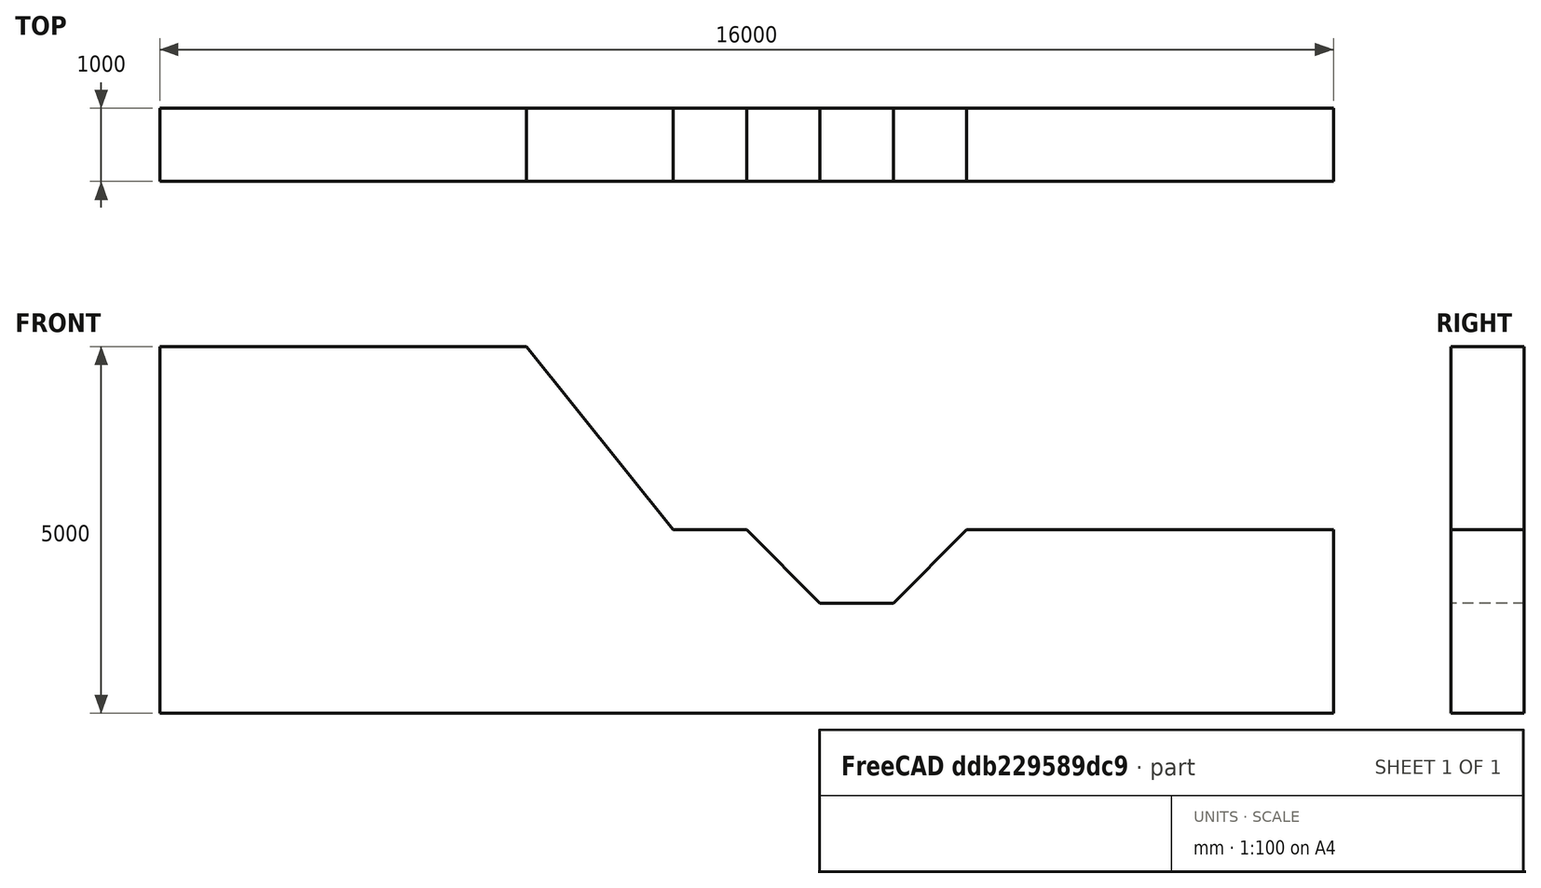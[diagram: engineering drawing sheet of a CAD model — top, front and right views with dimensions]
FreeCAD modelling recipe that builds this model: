
FCSTD DOCUMENT  (FreeCAD 1.0R39109 (Git))
Label: Embankment_with_Ditch_Example
License: All rights reserved
LicenseURL: http://en.wikipedia.org/wiki/All_rights_reserved
objects: Fem::FemMeshObjectPython×3, Fem::FemResultObjectPython×2, Sketcher::SketchObject×1, Part::Extrusion×1, Fem::FemSolverObjectPython×1, App::MaterialObjectPython×1, Fem::ConstraintFixed×1, Fem::ConstraintDisplacement×1, Fem::FemAnalysis×1
note: 3 computed .brp shape members not serialized (recipe doc carries the construction recipe); baked Part::Feature solids carry a one-line shape summary decoded from their .brp

FEATURE [Sketcher::SketchObject] Sketch
  ArcFitTolerance = 0
  FullyConstrained = true
  MakeInternals = false
  Placement = pos=(0,0,0) rot=(1,0,0;1.5708rad)
  sketch-geometry (10):
    g0: LineSegment StartX=0 StartY=0 StartZ=0 EndX=16000 EndY=0 EndZ=0
    g1: LineSegment StartX=0 StartY=0 StartZ=0 EndX=0 EndY=5000 EndZ=0
    g2: LineSegment StartX=0 StartY=5000 StartZ=0 EndX=5000 EndY=5000 EndZ=0
    g3: LineSegment StartX=5000 StartY=5000 StartZ=0 EndX=7000 EndY=2500 EndZ=0
    g4: LineSegment StartX=7000 StartY=2500 StartZ=0 EndX=8000 EndY=2500 EndZ=0
    g5: LineSegment StartX=8000 StartY=2500 StartZ=0 EndX=9000 EndY=1500 EndZ=0
    g6: LineSegment StartX=9000 StartY=1500 StartZ=0 EndX=10000 EndY=1500 EndZ=0
    g7: LineSegment StartX=10000 StartY=1500 StartZ=0 EndX=11000 EndY=2500 EndZ=0
    g8: LineSegment StartX=11000 StartY=2500 StartZ=0 EndX=16000 EndY=2500 EndZ=0
    g9: LineSegment StartX=16000 StartY=2500 StartZ=0 EndX=16000 EndY=0 EndZ=0
  constraints (29):
    c: Coincident(g0,g-1)
    c: PointOnObject(g0,g-1)
    c: Coincident(g1,g0)
    c: PointOnObject(g1,g-2)
    c: Coincident(g2,g1)
    c: Horizontal(g2)
    c: Distance(g1) = 5000
    c: Distance(g0) = 16000
    c: Distance(g2) = 5000
    c: Coincident(g3,g2)
    c: Coincident(g4,g3)
    c: Horizontal(g4)
    c: Coincident(g5,g4)
    c: Coincident(g6,g5)
    c: Horizontal(g6)
    c: Coincident(g8,g7)
    c: Horizontal(g8)
    c: Coincident(g9,g8)
    c: Coincident(g9,g0)
    c: DistanceY(g3,g2) = 2500
    c: DistanceY(g5,g4) = 1000
    c: DistanceY(g6,g7) = 1000
    c: DistanceX(g2,g3) = 2000
    c: DistanceX(g4,g5) = 1000
    c: DistanceX(g6,g7) = 1000
    c: Distance(g6) = 1000
    c: Coincident(g6,g7)
    c: Distance(g4) = 1000
    c: Distance(g8) = 5000
FEATURE [Part::Extrusion] Extrude
  Base = -> Sketch
  Dir = (0,-1,2e-16)
  DirMode = 2
  FaceMakerClass = Part::FaceMakerBullseye
  FaceMakerMode = 3
  LengthFwd = 1000
  LengthRev = 0
  Solid = true
  Symmetric = false
FEATURE [Fem::FemSolverObjectPython] SolverCcxTools  # FEM object (typed FeaturePython)
  AnalysisType = 0
  BeamReducedIntegration = true
  BeamShellResultOutput3D = false
  BucklingFactors = 1
  EigenmodeHighLimit = 1000000
  EigenmodeLowLimit = 0
  EigenmodesCount = 10
  GeometricalNonlinearity = 0
  IterationsControlParameterCutb = 0.25,0.5,0.75,0.85,,,1.5,
  IterationsControlParameterIter = 4,8,9,200,10,400,,200,,
  IterationsControlParameterTimeUse = false
  IterationsMaximum = 2000
  IterationsUserDefinedIncrementations = false
  IterationsUserDefinedTimeStepLength = false
  MaterialNonlinearity = 0
  MatrixSolverType = 0
  ModelSpace = 0
  OutputFrequency = 1
  SplitInputWriter = false
  ThermoMechSteadyState = true
  ThermoMechType = 0
  TimeEnd = 1
  TimeInitialStep = 0.01
  TimeMaximumStep = 1
  TimeMinimumStep = 1e-05
FEATURE [Fem::FemMeshObjectPython] FEMMeshGmsh  # FEM object (typed FeaturePython)
  Algorithm2D = 0
  Algorithm3D = 0
  CharacteristicLengthMax = 1000
  CharacteristicLengthMin = 0
  CoherenceMesh = true
  ElementDimension = 0
  ElementOrder = 1
  GeometryTolerance = 1e-06
  GroupsOfNodes = false
  HighOrderOptimize = 0
  MeshSizeFromCurvature = 12
  OptimizeNetgen = false
  OptimizeStd = true
  RecombinationAlgorithm = 0
  Recombine3DAll = false
  RecombineAll = false
  SecondOrderLinear = false
  Shape = -> Extrude
  SubdivisionAlgorithm = 0
FEATURE [App::MaterialObjectPython] MaterialSolid  # material (typed FeaturePython)
  Category = 0
  Material = Density=2000.0000000000002 kg/m^3; Name=NoName; PoissonRatio=0.45; YoungsModulus=5000.0 kPa
  References = -> [Extrude]
FEATURE [Fem::ConstraintFixed] ConstraintFixed
  NormalDirection = (0,-2e-16,-1)
  Normals = (52) [(0,-2.22045e-16,-1),(0,-2.22045e-16,-1),(0,-2.22045e-16,-1),(0,-2.22045e-16,-1),(0,-2.22045e-16,-1),(0,-2.22045e-16,-1),(0,-2.22045e-16,-1),+45 more]
  Points = (52) [(0,-1000,2.22045e-13),(4000,-1000,2.22045e-13),(8000,-1000,2.22045e-13),(12000,-1000,2.22045e-13),(16000,-1000,2.22045e-13),(0,-666.667,1.4803e-13),+46 more]
  References = -> [Extrude]
  Suppressed = false
FEATURE [Fem::ConstraintDisplacement] ConstraintDisplacement
  NormalDirection = (0,-1,0)
  Normals = (28) [(0,-1,0),(0,-1,0),(0,-1,0),(0,-1,0),(0,-1,0),(0,-1,0),(0,-1,0),(0,-1,0),(0,-1,0),(0,-1,0),(0,-1,0),(0,-1,0),(0,-1,0),(0,-1,0),(0,1,0),(0,1,0),(0,1,0),+11 more]
  Points = (28) [(0,-1000,2.22045e-13),(0,-1000,1666.67),(0,-1000,3333.33),(0,-1000,5000),(4000,-1000,2.22045e-13),(4000,-1000,1666.67),(4000,-1000,3333.33),+21 more]
  References = -> [Extrude]
  Suppressed = false
  hasXFormula = false
  hasYFormula = false
  hasZFormula = false
  rotxFree = true
  rotyFree = true
  rotzFree = true
  useFlowSurfaceForce = false
  xDisplacement = 0
  xFree = true
  xRotation = 0
  yDisplacement = 0
  yFree = false
  yRotation = 0
  zDisplacement = 0
  zFree = true
  zRotation = 0
FEATURE [Fem::FemMeshObjectPython] Result_Mesh_Volume  # FEM object (typed FeaturePython)
FEATURE [Fem::FemResultObjectPython] ResultMechanical  label="ElasticPlasticDisplacementResults"  # FEM object (typed FeaturePython)
  CriticalStrainRatio = [0,0,0,0,0,0,0,0,2.42983e-10,6.16908e-12,5.22149e-12,1.98636e-12,1.20943e-16,1.33212e-15,3.37437e-15,2.31998e-15,0,0,8.99629e-10,1.06352e-09,0,0,0,2.75474e-18,1.20063e-15,2.91501e-15,7.42428e-14,5.97273e-13,5.72757e-14,6.13416e-13,+1388 more]
  DisplacementLengths = [0,0,0,0,0,0,0.0675648,0.0696649,8.61495,12.4684,48.3695,48.2212,40.4954,40.5376,38.9764,39.0359,28.1649,28.1554,0,0,0,0,0,0,0,0,0,0,0,0,0,0,0,0,0,0,0,0,0,0,0,0,0,0,0,0,0,0,0,0,0,0,0,0,0,0,0,0,0,0,0,0,0,0,0,0,0,0,0,0,0,0,0,0,0,0,0,0,0,0,0,0,+1336 more]
  DisplacementVectors = (1418) [(0,0,0),(0,0,0),(0,0,0),(0,0,0),(0,0,0),(0,0,0),(0.0554836,0,0.0385561),(0.0530245,0,0.0451841),(2.76651,0,8.15866),(4.3747,0,11.6757),+1408 more]
  Eigenmode = 0
  EigenmodeFrequency = 0
  Mesh = -> Result_Mesh_Volume
  NodeNumbers = [1,2,3,4,5,6,7,8,9,10,11,12,13,14,15,16,17,18,19,20,21,22,23,24,25,26,27,28,29,30,31,32,33,34,35,36,37,38,39,40,41,42,43,44,45,46,47,48,49,50,51,52,53,54,55,56,57,58,59,60,61,62,63,64,65,66,67,68,69,+1349 more]
  NodeStressXX = [-0.0243961,-0.024347,-0.0128124,-0.0127902,0.00099877,0.0010043,-0.00214398,-0.00192855,-0.0129446,-0.0140504,-0.0152387,-0.0150952,-0.00378372,-0.00434693,-0.0119624,-0.0128338,-0.00492271,-0.0045627,0.0289763,0.0289847,-0.0243716,+1397 more]
  NodeStressXY = [-0.000159539,0.000157471,8.78e-05,-8.50787e-05,3.49759e-05,-4.02729e-05,-0.000174176,2.61487e-05,0.000294874,-0.000166784,-1.36269e-05,0.000148182,0.000668704,0.000338497,1.82087e-05,-0.000196398,0.000288991,1.95147e-05,-0.000306088,+1399 more]
  NodeStressXZ = [-0.00241993,-0.00241528,0.00125885,0.00125896,0.00233353,0.00235979,-0.00113678,-0.000748649,-0.00325613,-0.00244191,0.00250177,0.00325038,0.00111477,0.0019482,0.00444745,0.00461718,0.00273077,0.00289478,-0.00454733,-0.0046364,-0.0024176,+1397 more]
  NodeStressYY = [-0.0221145,-0.0220862,-0.0117029,-0.0116901,0.00059661,0.000603752,-0.00144163,-0.00121294,-0.00917404,-0.0101033,-0.0108979,-0.0110659,-0.00296808,-0.00101352,-0.00816128,-0.0108997,-0.00269623,-0.00329485,0.0271222,0.0263927,-0.0221003,+1397 more]
  NodeStressYZ = [-0.000158389,0.00016654,-8.80079e-05,8.9625e-05,4.05562e-05,-3.98936e-05,0.000338661,9.27179e-05,0.000423613,-0.000875109,0.00059401,-8.28474e-05,0.000115806,-0.000804275,-7.19199e-05,0.000394603,-0.000117064,0.000209199,-0.000477833,+1399 more]
  NodeStressZZ = [-0.0247875,-0.0247841,-0.0132232,-0.0132102,0.000383708,0.000376666,-0.000695995,-0.000848375,-0.00492929,-0.00527106,-0.0059432,-0.00686406,-0.000378918,-0.00142703,-0.0074521,-0.00919909,-0.00209459,-0.00212633,0.0234852,0.0235883,+1398 more]
  Peeq = [0,0,0,0,0,0,0,0,0.363828,0.362103,0.525574,0.494688,0.000244618,0.00290423,0.0262096,0.0246402,0,0,0.261558,0.267558,0,0,0,0.00158418,0.0184713,0.0813623,0.18187,0.271544,0.314664,0.267389,0.138928,0.0218066,0,0,0,0,0,0,0.00079209,+1379 more]
  ResultType = Fem::ResultMechanical
  Stats = [-0.288825,49.0125,-1.42828,1.53232,-37.0419,32.2236,0,55.2596,0.00100772,0.01,0,0,0,0,0,0,0,0,0,0.564306,0,0.000184573,0,0,0,0]
  Temperature = [0,0,0,0,0,0,0,0,2.42983e-10,6.16908e-12,5.22149e-12,1.98636e-12,1.20943e-16,1.33212e-15,3.37437e-15,2.31998e-15,0,0,8.99629e-10,1.06352e-09,0,0,0,2.75474e-18,1.20063e-15,2.91501e-15,7.42428e-14,5.97273e-13,5.72757e-14,6.13416e-13,+1388 more]
  Time = 0
  vonMises = [0.00745978,0.00737079,0.00401085,0.0040026,0.00502197,0.00506388,0.00967902,0.00410237,0.01,0.01,0.01,0.01,0.01,0.01,0.01,0.01,0.00706963,0.00638497,0.01,0.01,0.00741528,0.00400673,0.00987286,0.01,0.01,0.01,0.01,0.01,0.01,0.01,0.01,0.01,+1386 more]
FEATURE [Fem::FemMeshObjectPython] Result_Mesh_Volume001  # FEM object (typed FeaturePython)
FEATURE [Fem::FemResultObjectPython] ResultMechanical001  label="ElasticDisplacementResults"  # FEM object (typed FeaturePython)
  DisplacementLengths = [0,0,0,0,0,0,2.34696,2.34891,1.32311,1.29376,6.28617,6.25235,10.0467,10.0464,11.7714,11.847,18.5415,18.5418,0,0,0,0,0,0,0,0,0,0,0,0,0,0,0,0,0,0,0,0,0,0,0,0,0,0,0,0,0,0,0,0,0,0,0,0,0,0,0,0,0,0,0,0,0,0,0,0,0,0,0,0,0,0,0,0,0,0,0,0,0,0,0,0,0,0,+1334 more]
  DisplacementVectors = (1418) [(0,0,0),(0,0,0),(0,0,0),(0,0,0),(0,0,0),(0,0,0),(0.721996,0,-2.23314),(0.718477,0,-2.23633),(1.23963,0,0.462532),(1.19994,0,0.483709),+1408 more]
  Eigenmode = 0
  EigenmodeFrequency = 0
  Mesh = -> Result_Mesh_Volume001
  NodeNumbers = [1,2,3,4,5,6,7,8,9,10,11,12,13,14,15,16,17,18,19,20,21,22,23,24,25,26,27,28,29,30,31,32,33,34,35,36,37,38,39,40,41,42,43,44,45,46,47,48,49,50,51,52,53,54,55,56,57,58,59,60,61,62,63,64,65,66,67,68,69,+1349 more]
  ResultType = Fem::ResultMechanical
  Stats = [-1.46755,11.4557,-0.0651627,0.0404512,-20.3262,1.17973,0,20.9144,0,0,0,0,0,0,0,0,0,0,0,0,0,0,0,0,0,0]
  Time = 0
FEATURE [Fem::FemAnalysis] Analysis
  Group = -> [SolverCcxTools,FEMMeshGmsh,MaterialSolid,ConstraintFixed,ConstraintDisplacement,ResultMechanical,ResultMechanical001]
